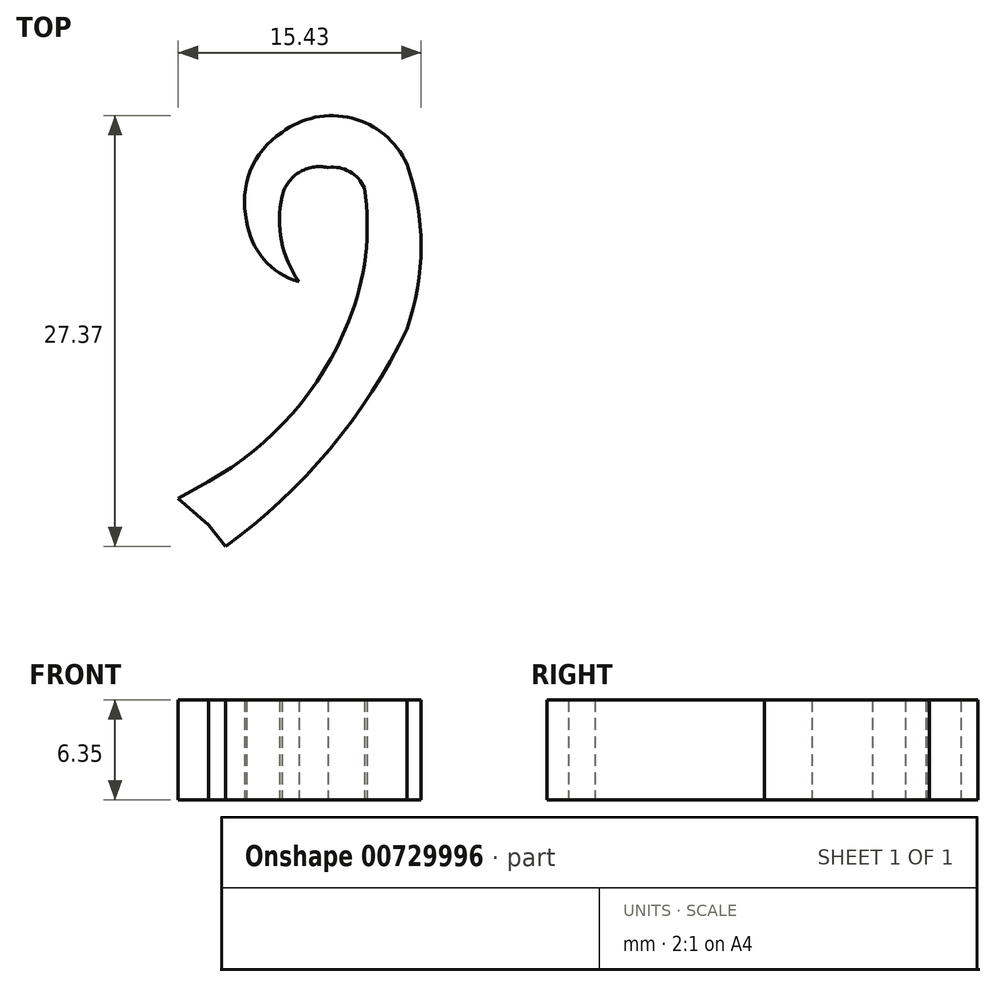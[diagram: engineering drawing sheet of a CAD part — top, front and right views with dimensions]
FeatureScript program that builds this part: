
annotation { "Feature Type Name" : "Feature", "Feature Type Description" : "" }
export const myFeature = defineFeature(function(context is Context, id is Id, definition is map)
    precondition{}
    {
        {
            var Q0;
            Q0=qCreatedBy(makeId("Top.planeOp"),FACE);
            var sketch = newSketch(context, id + "F0", { "sketchPlane" : qUnion([Q0])});
            skLineSegment(sketch, "E0.bottom", {"start": v(0, 0) * mm, "end": v(-381, 0) * mm});
            skLineSegment(sketch, "E0.top", {"start": v(0, 1066.8) * mm, "end": v(-381, 1066.8) * mm});
            skLineSegment(sketch, "E0.left", {"start": v(0, 0) * mm, "end": v(0, 1066.8) * mm});
            skLineSegment(sketch, "E0.right", {"start": v(-381, 0) * mm, "end": v(-381, 1066.8) * mm});
            skLineSegment(sketch, "E1", {"start": v(-119.77, 0) * mm, "end": v(-119.77, 1066.8) * mm});
            skLineSegment(sketch, "E2", {"start": v(-87.35, 911.34) * mm, "end": v(-87.35, 389.06) * mm});
            skArc(sketch, "E3", {"start": v(-87.35, 389.06) * mm, "mid": v(-85.1, 378.45) * mm, "end": v(-78.75, 369.65) * mm});
            skLineSegment(sketch, "E4", {"start": v(-78.75, 369.65) * mm, "end": v(-78.75, 351.02) * mm});
            skArc(sketch, "E5", {"start": v(-78.75, 351.02) * mm, "mid": v(-91.55, 336.49) * mm, "end": v(-98.09, 318.26) * mm});
            skLineSegment(sketch, "E6", {"start": v(-98.09, 318.26) * mm, "end": v(-98.09, 292.1) * mm});
            skLineSegment(sketch, "E7", {"start": v(-98.09, 292.1) * mm, "end": v(-98.09, 228.36) * mm});
            skLineSegment(sketch, "E8", {"start": v(-111.46, 23.32) * mm, "end": v(-111.46, 213.76) * mm});
            skPoint(sketch, "E9", {"position": v(-107.65, 51.89) * mm});
            skArc(sketch, "E10", {"start": v(-98.09, 228.36) * mm, "mid": v(-107.6, 223.66) * mm, "end": v(-111.46, 213.76) * mm});
            skLineSegment(sketch, "E11", {"start": v(-115, -7.78) * mm, "end": v(-115, 18.47) * mm});
            skArc(sketch, "E12", {"start": v(-111.46, 23.32) * mm, "mid": v(-113.78, 21.3) * mm, "end": v(-115, 18.47) * mm});
            skLineSegment(sketch, "E13.MirrorCS", {"start": v(-124.53, -7.78) * mm, "end": v(-124.53, 18.47) * mm});
            skArc(sketch, "E14.MirrorCS", {"start": v(-128.07, 23.32) * mm, "mid": v(-125.75, 21.3) * mm, "end": v(-124.53, 18.47) * mm});
            skLineSegment(sketch, "E15.MirrorCS", {"start": v(-128.07, 23.32) * mm, "end": v(-128.07, 213.76) * mm});
            skArc(sketch, "E16.MirrorCS", {"start": v(-141.45, 228.36) * mm, "mid": v(-131.92, 223.66) * mm, "end": v(-128.07, 213.76) * mm});
            skLineSegment(sketch, "E17.MirrorCS", {"start": v(-141.45, 292.1) * mm, "end": v(-141.45, 228.36) * mm});
            skLineSegment(sketch, "E18.MirrorCS", {"start": v(-141.45, 318.26) * mm, "end": v(-141.45, 292.1) * mm});
            skArc(sketch, "E19.MirrorCS", {"start": v(-160.78, 351.02) * mm, "mid": v(-147.98, 336.49) * mm, "end": v(-141.45, 318.26) * mm});
            skLineSegment(sketch, "E20.MirrorCS", {"start": v(-160.78, 369.65) * mm, "end": v(-160.78, 351.02) * mm});
            skArc(sketch, "E21.MirrorCS", {"start": v(-152.18, 389.06) * mm, "mid": v(-154.43, 378.45) * mm, "end": v(-160.78, 369.65) * mm});
            skLineSegment(sketch, "E22.MirrorCS", {"start": v(-152.18, 911.34) * mm, "end": v(-152.18, 389.06) * mm});
            skArc(sketch, "E23", {"start": v(-87.35, 911.34) * mm, "mid": v(-95.54, 990.21) * mm, "end": v(-119.77, 1065.71) * mm});
            skArc(sketch, "E24.MirrorCS", {"start": v(-152.18, 911.34) * mm, "mid": v(-144, 990.21) * mm, "end": v(-119.77, 1065.71) * mm});
            skLineSegment(sketch, "E25", {"start": v(-115, -7.78) * mm, "end": v(-124.53, -7.78) * mm});
            skLineSegment(sketch, "E26", {"start": v(-98.09, 292.1) * mm, "end": v(-94.05, 290.7) * mm});
            skLineSegment(sketch, "E27", {"start": v(-94.05, 290.7) * mm, "end": v(-94.05, 280.07) * mm});
            skArc(sketch, "E28", {"start": v(-96.44, 279.4) * mm, "mid": v(-95.17, 279.47) * mm, "end": v(-94.05, 280.07) * mm});
            skLineSegment(sketch, "E29", {"start": v(-96.44, 279.4) * mm, "end": v(-96.44, 257.55) * mm});
            skArc(sketch, "E30", {"start": v(-96.44, 257.55) * mm, "mid": v(-95.25, 252.18) * mm, "end": v(-91.9, 247.81) * mm});
            skArc(sketch, "E31", {"start": v(-65.85, 231.96) * mm, "mid": v(-76.62, 242.37) * mm, "end": v(-89.75, 249.6) * mm});
            skArc(sketch, "E32", {"start": v(-65.85, 231.96) * mm, "mid": v(-60.2, 239.8) * mm, "end": v(-56.84, 248.85) * mm});
            skLineSegment(sketch, "E33", {"start": v(-91.9, 247.81) * mm, "end": v(-89.75, 249.6) * mm});
            skLineSegment(sketch, "E34", {"start": v(-56.84, 248.85) * mm, "end": v(-4.44, 267.15) * mm});
            skArc(sketch, "E35", {"start": v(-47.43, 198.86) * mm, "mid": v(-19.12, 228.71) * mm, "end": v(-4.44, 267.15) * mm});
            skLineSegment(sketch, "E36", {"start": v(-47.43, 198.86) * mm, "end": v(-48.35, 180.08) * mm});
            skArc(sketch, "E37", {"start": v(-48.35, 180.08) * mm, "mid": v(-69.95, 201.45) * mm, "end": v(-98.6, 211.59) * mm});
            skArc(sketch, "E38", {"start": v(-98.6, 211.59) * mm, "mid": v(-107.22, 209.5) * mm, "end": v(-111.46, 201.7) * mm});
            skLineSegment(sketch, "E39.MirrorCS", {"start": v(-141.45, 292.1) * mm, "end": v(-145.48, 290.7) * mm});
            skLineSegment(sketch, "E40.MirrorCS", {"start": v(-145.48, 290.7) * mm, "end": v(-145.48, 280.07) * mm});
            skArc(sketch, "E41.MirrorCS", {"start": v(-143.1, 279.4) * mm, "mid": v(-144.36, 279.47) * mm, "end": v(-145.48, 280.07) * mm});
            skLineSegment(sketch, "E42.MirrorCS", {"start": v(-143.1, 279.4) * mm, "end": v(-143.1, 257.55) * mm});
            skArc(sketch, "E43.MirrorCS", {"start": v(-143.1, 257.55) * mm, "mid": v(-144.28, 252.18) * mm, "end": v(-147.62, 247.81) * mm});
            skLineSegment(sketch, "E44.MirrorCS", {"start": v(-147.62, 247.81) * mm, "end": v(-149.78, 249.6) * mm});
            skArc(sketch, "E45.MirrorCS", {"start": v(-173.68, 231.96) * mm, "mid": v(-162.9, 242.37) * mm, "end": v(-149.78, 249.6) * mm});
            skArc(sketch, "E46.MirrorCS", {"start": v(-173.68, 231.96) * mm, "mid": v(-179.34, 239.8) * mm, "end": v(-182.69, 248.85) * mm});
            skLineSegment(sketch, "E47.MirrorCS", {"start": v(-182.69, 248.85) * mm, "end": v(-235.1, 267.15) * mm});
            skArc(sketch, "E48.MirrorCS", {"start": v(-192.1, 198.86) * mm, "mid": v(-220.4, 228.71) * mm, "end": v(-235.1, 267.15) * mm});
            skLineSegment(sketch, "E49.MirrorCS", {"start": v(-192.1, 198.86) * mm, "end": v(-191.18, 180.08) * mm});
            skArc(sketch, "E50.MirrorCS", {"start": v(-191.18, 180.08) * mm, "mid": v(-169.58, 201.45) * mm, "end": v(-140.94, 211.59) * mm});
            skArc(sketch, "E51.MirrorCS", {"start": v(-140.94, 211.59) * mm, "mid": v(-132.31, 209.5) * mm, "end": v(-128.07, 201.7) * mm});
            skPoint(sketch, "E52", {"position": v(-158.27, 189.47) * mm});
            skPoint(sketch, "E52.positionSnap0", {"position": v(-191.64, 189.47) * mm});
            skPoint(sketch, "E53", {"position": v(-80.65, 189.97) * mm});
            skPoint(sketch, "E54", {"position": v(-80.65, 199.13) * mm});
            skPoint(sketch, "E55", {"position": v(-158.64, 199.13) * mm});
            skPoint(sketch, "E56", {"position": v(-134.84, 180.82) * mm});
            skPoint(sketch, "E57", {"position": v(-103.72, 180.82) * mm});
            skPoint(sketch, "E58", {"position": v(-131.92, 223.66) * mm});
            skPoint(sketch, "E59", {"position": v(-106.03, 225.14) * mm});
            skPoint(sketch, "E60", {"position": v(-134.14, 224.32) * mm});
            skLineSegment(sketch, "E61", {"start": v(-140.94, 211.59) * mm, "end": v(-98.6, 211.59) * mm});
            skLineSegment(sketch, "E62", {"start": v(-147.62, 247.81) * mm, "end": v(-141.45, 242.44) * mm});
            skLineSegment(sketch, "E63", {"start": v(-91.9, 247.81) * mm, "end": v(-98.09, 242.37) * mm});
            skPoint(sketch, "E63.endSnap0", {"position": v(-76.62, 242.37) * mm});
            skLineSegment(sketch, "E64", {"start": v(-141.45, 242.44) * mm, "end": v(-119.77, 214.96) * mm});
            skLineSegment(sketch, "E65", {"start": v(-119.77, 214.96) * mm, "end": v(-98.09, 242.37) * mm});
            skArc(sketch, "E66", {"start": v(-158.64, 199.13) * mm, "mid": v(-148.72, 203.85) * mm, "end": v(-140.94, 211.59) * mm});
            skLineSegment(sketch, "E67", {"start": v(-158.64, 199.13) * mm, "end": v(-158.64, 189.92) * mm});
            skLineSegment(sketch, "E68", {"start": v(-158.64, 189.92) * mm, "end": v(-135.77, 180.06) * mm});
            skLineSegment(sketch, "E69", {"start": v(-135.77, 180.06) * mm, "end": v(-119.77, 180.06) * mm});
            skArc(sketch, "E70.MirrorCS", {"start": v(-80.9, 199.13) * mm, "mid": v(-90.8, 203.85) * mm, "end": v(-98.6, 211.59) * mm});
            skLineSegment(sketch, "E71.MirrorCS", {"start": v(-80.9, 199.13) * mm, "end": v(-80.9, 189.92) * mm});
            skLineSegment(sketch, "E72.MirrorCS", {"start": v(-80.9, 189.92) * mm, "end": v(-103.77, 180.06) * mm});
            skLineSegment(sketch, "E73.MirrorCS", {"start": v(-103.77, 180.06) * mm, "end": v(-119.77, 180.06) * mm});
            skLineSegment(sketch, "E74", {"start": v(-119.77, 3.08) * mm, "end": v(-128.68, 3.08) * mm});
            skLineSegment(sketch, "E75", {"start": v(-128.68, 3.08) * mm, "end": v(-136.74, 25.23) * mm});
            skLineSegment(sketch, "E76", {"start": v(-133.63, 47.01) * mm, "end": v(-145.7, 37.5) * mm});
            skLineSegment(sketch, "E77", {"start": v(-133.63, 47.01) * mm, "end": v(-133.63, 51.22) * mm});
            skLineSegment(sketch, "E78", {"start": v(-133.63, 51.22) * mm, "end": v(-119.77, 51.22) * mm});
            skArc(sketch, "E79", {"start": v(-145.7, 37.5) * mm, "mid": v(-142.4, 30.5) * mm, "end": v(-136.74, 25.23) * mm});
            skLineSegment(sketch, "E80.MirrorCS", {"start": v(-105.9, 51.22) * mm, "end": v(-119.77, 51.22) * mm});
            skLineSegment(sketch, "E81.MirrorCS", {"start": v(-105.9, 47.01) * mm, "end": v(-105.9, 51.22) * mm});
            skLineSegment(sketch, "E82.MirrorCS", {"start": v(-105.9, 47.01) * mm, "end": v(-93.82, 37.5) * mm});
            skArc(sketch, "E83.MirrorCS", {"start": v(-93.82, 37.5) * mm, "mid": v(-97.14, 30.5) * mm, "end": v(-102.8, 25.23) * mm});
            skLineSegment(sketch, "E84.MirrorCS", {"start": v(-110.85, 3.08) * mm, "end": v(-102.8, 25.23) * mm});
            skLineSegment(sketch, "E85.MirrorCS", {"start": v(-119.77, 3.08) * mm, "end": v(-110.85, 3.08) * mm});
            skLineSegment(sketch, "E86", {"start": v(-136.53, 236.2) * mm, "end": v(-125.07, 253.32) * mm});
            skLineSegment(sketch, "E87", {"start": v(-125.07, 253.32) * mm, "end": v(-125.07, 262.84) * mm});
            skLineSegment(sketch, "E88", {"start": v(-125.07, 262.84) * mm, "end": v(-119.77, 269.55) * mm});
            skLineSegment(sketch, "E89.MirrorCS", {"start": v(-114.46, 262.84) * mm, "end": v(-119.77, 269.55) * mm});
            skLineSegment(sketch, "E90.MirrorCS", {"start": v(-114.46, 253.32) * mm, "end": v(-114.46, 262.84) * mm});
            skLineSegment(sketch, "E91.MirrorCS", {"start": v(-103, 236.2) * mm, "end": v(-114.46, 253.32) * mm});
            skLineSegment(sketch, "E92", {"start": v(-123.7, 264.57) * mm, "end": v(-134.04, 277.13) * mm});
            skLineSegment(sketch, "E93", {"start": v(-134.04, 277.13) * mm, "end": v(-134.04, 282.26) * mm});
            skLineSegment(sketch, "E94", {"start": v(-134.04, 282.26) * mm, "end": v(-132.68, 283.98) * mm});
            skLineSegment(sketch, "E95", {"start": v(-132.68, 283.98) * mm, "end": v(-132.68, 329.29) * mm});
            skLineSegment(sketch, "E96", {"start": v(-141.45, 292.1) * mm, "end": v(-132.68, 294.94) * mm});
            skArc(sketch, "E97", {"start": v(-140.37, 241.07) * mm, "mid": v(-133.74, 247.26) * mm, "end": v(-128.85, 254.9) * mm});
            skArc(sketch, "E98", {"start": v(-128.85, 254.9) * mm, "mid": v(-127.94, 260.13) * mm, "end": v(-128.85, 265.36) * mm});
            skArc(sketch, "E99", {"start": v(-128.85, 265.36) * mm, "mid": v(-132.34, 268.28) * mm, "end": v(-136.78, 267.37) * mm});
            skArc(sketch, "E100", {"start": v(-136.78, 267.37) * mm, "mid": v(-138.8, 264.91) * mm, "end": v(-139.02, 261.74) * mm});
            skArc(sketch, "E101", {"start": v(-139.02, 261.74) * mm, "mid": v(-137.94, 259.32) * mm, "end": v(-135.7, 257.9) * mm});
            skArc(sketch, "E102", {"start": v(-136.78, 263.29) * mm, "mid": v(-136.8, 260.48) * mm, "end": v(-135.7, 257.9) * mm});
            skArc(sketch, "E103", {"start": v(-133.86, 265.13) * mm, "mid": v(-135.7, 264.82) * mm, "end": v(-136.78, 263.29) * mm});
            skArc(sketch, "E104", {"start": v(-131.55, 263.82) * mm, "mid": v(-132.48, 264.88) * mm, "end": v(-133.86, 265.13) * mm});
            skArc(sketch, "E105", {"start": v(-132.55, 255.35) * mm, "mid": v(-131.47, 259.52) * mm, "end": v(-131.55, 263.82) * mm});
            skArc(sketch, "E106", {"start": v(-141.45, 245.19) * mm, "mid": v(-136.12, 249.5) * mm, "end": v(-132.55, 255.35) * mm});
            skLineSegment(sketch, "E107", {"start": v(-141.45, 245.19) * mm, "end": v(-143.37, 244.11) * mm});
            skArc(sketch, "E108.MirrorCS", {"start": v(-99.16, 241.07) * mm, "mid": v(-105.8, 247.26) * mm, "end": v(-110.68, 254.9) * mm});
            skArc(sketch, "E109.MirrorCS", {"start": v(-98.09, 245.19) * mm, "mid": v(-103.41, 249.5) * mm, "end": v(-106.98, 255.35) * mm});
            skLineSegment(sketch, "E110.MirrorCS", {"start": v(-98.09, 245.19) * mm, "end": v(-96.16, 244.11) * mm});
            skArc(sketch, "E111.MirrorCS", {"start": v(-110.68, 254.9) * mm, "mid": v(-111.59, 260.13) * mm, "end": v(-110.68, 265.36) * mm});
            skArc(sketch, "E112.MirrorCS", {"start": v(-106.98, 255.35) * mm, "mid": v(-108.06, 259.52) * mm, "end": v(-107.98, 263.82) * mm});
            skArc(sketch, "E113.MirrorCS", {"start": v(-107.98, 263.82) * mm, "mid": v(-107.05, 264.88) * mm, "end": v(-105.67, 265.13) * mm});
            skArc(sketch, "E114.MirrorCS", {"start": v(-110.68, 265.36) * mm, "mid": v(-107.2, 268.28) * mm, "end": v(-102.75, 267.37) * mm});
            skArc(sketch, "E115.MirrorCS", {"start": v(-102.75, 267.37) * mm, "mid": v(-100.74, 264.91) * mm, "end": v(-100.51, 261.74) * mm});
            skArc(sketch, "E116.MirrorCS", {"start": v(-100.51, 261.74) * mm, "mid": v(-101.59, 259.32) * mm, "end": v(-103.83, 257.9) * mm});
            skArc(sketch, "E117.MirrorCS", {"start": v(-102.75, 263.29) * mm, "mid": v(-102.72, 260.48) * mm, "end": v(-103.83, 257.9) * mm});
            skArc(sketch, "E118.MirrorCS", {"start": v(-105.67, 265.13) * mm, "mid": v(-103.83, 264.82) * mm, "end": v(-102.75, 263.29) * mm});
            skLineSegment(sketch, "E119.MirrorCS", {"start": v(-115.83, 264.57) * mm, "end": v(-105.49, 277.13) * mm});
            skLineSegment(sketch, "E120.MirrorCS", {"start": v(-105.49, 277.13) * mm, "end": v(-105.49, 282.26) * mm});
            skLineSegment(sketch, "E121.MirrorCS", {"start": v(-105.49, 282.26) * mm, "end": v(-106.85, 283.98) * mm});
            skLineSegment(sketch, "E122.MirrorCS", {"start": v(-106.85, 283.98) * mm, "end": v(-106.85, 329.29) * mm});
            skLineSegment(sketch, "E123.MirrorCS", {"start": v(-98.09, 292.1) * mm, "end": v(-106.85, 294.94) * mm});
            skLineSegment(sketch, "E124", {"start": v(-103, 236.2) * mm, "end": v(-102.98, 236.18) * mm});
            skSolve(sketch);
        }
        {
            var Q0;
            {var subQ3=sQuery(id+"F0.wireOp",EDGE,"E97");Q0=makeQuery(id+"F0.imprint","IMPRINT",FACE,{"disambiguationData":[TD([[makeQuery(id+"F0.imprint","IMPRINT",EDGE,{"derivedFrom":subQ3}),1.0]])]});}
            var Q1;
            {var subQ3=sQuery(id+"F0.wireOp",EDGE,"E107");Q1=makeQuery(id+"F0.imprint","IMPRINT",FACE,{"disambiguationData":[TD([[makeQuery(id+"F0.imprint","IMPRINT",EDGE,{"derivedFrom":subQ3}),1.0]])]});}
            extrude(context, id + "F1", {"entities" : qUnion([Q0, Q1]), "depth" : 6.35 * mm, "offsetDistance" : 25.4 * mm});
        }
    });
